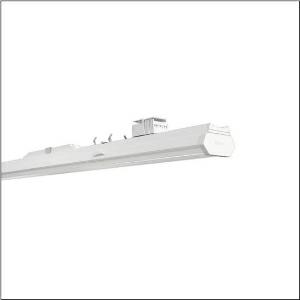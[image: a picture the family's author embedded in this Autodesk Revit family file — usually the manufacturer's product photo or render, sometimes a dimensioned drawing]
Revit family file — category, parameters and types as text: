
# Revit family: licross_r__11_protected_extreme_ho_51tp12dn4exle_25d9
name_source: partatom
category: Lighting Fixtures
units: mm (PartAtom-declared; Revit-internal decimal feet)

## family parameters
Cut with Voids When Loaded = No
Host = Face
Light Source = No
Part Type = Normal
Room Calculation Point = No
Round Connector Dimension = Use Diameter
Shared = No

## types (1)
- --- (1 x LED, 14070 lm, 86.1 W, 4000K)
    Apparent Load = 86 VA
    CIE Flux Codes = 70 91 97 98 100
    Color Rendering = 80
    Color Temperature = 4000K
    Default Elevation = 1800 mm
    Description = Licross® 11 Protected extreme HOluminaire insert, length: 1.500mm, width: 90mm, height: 101mm, LED rated luminous flux: 14.070lm, light colour: 840, control gear: DALI 2, control gear: ECG DALI, with plug, 5-pole, with phase selection, mains connection: 220..240V, AC, 50/60Hz, halogen-free wiring, primary optical cover: cover, of PMMA, light emission: direct with ceiling illumination distribution, protection rating (complete): IP64, insulation class (complete): insulation class I (protective earthing), certification: CE, ENEC, VDE, protection symbol: D if used in an environment with conductive dust loads with corresponding accessories, permissible ambient temperature for indoor applications: -25..+45°C, reducing of maximum allowable ambient temperature of 5°C with ceiling mounting, corresponds to IFS (International Featured Standards) requirements for safety and quality in the food industry, packaging unit: 1 piece
    Height = 92 mm
    Lamp = 1 x LED
    Lamp Light Flux = 14070 lm
    Lamp Power = 86.1 W
    Lamp count = 1
    Length = 1500 mm
    Luminous efficacy = 163 lm/W
    Manufacturer = Siteco
    ModVariant = No
    Model = 51TP12DN4EXLE
    Mounting Place = Ceiling
    Mounting Type = Pendant
    Number of Poles = 1
    OnlyDefault = Yes
    Power Factor = 1
    Product Name = Licross® 11 Protected extreme HO
    Product group = luminaire insert
    ProductGroupID = 902
    Protection Class = Protection class I
    Protection Degree = IP 64
    RLX_Detail_Level = 1
    RlxData = <blob elided: 23937 chars, md5=04e73499>
    Socket = socket
    Standby Power = 0 W
    System Light Flux = 14070 lm
    System Power = 86 W
    Type Comments = factory setting: luminous flux: 100 % | dim-lin: 254 | 485 mA
    Type Image = l_1256148.jpg
    URL = http://relux.com
    VarID = @adj_132794
    Voltage = 0 V
    Weight = 0.00 kg
    Width = 88 mm

## geometry (parser evidence)
native form markers: Blend x4, Sweep x11
no freeform markers — native parametric forms only
